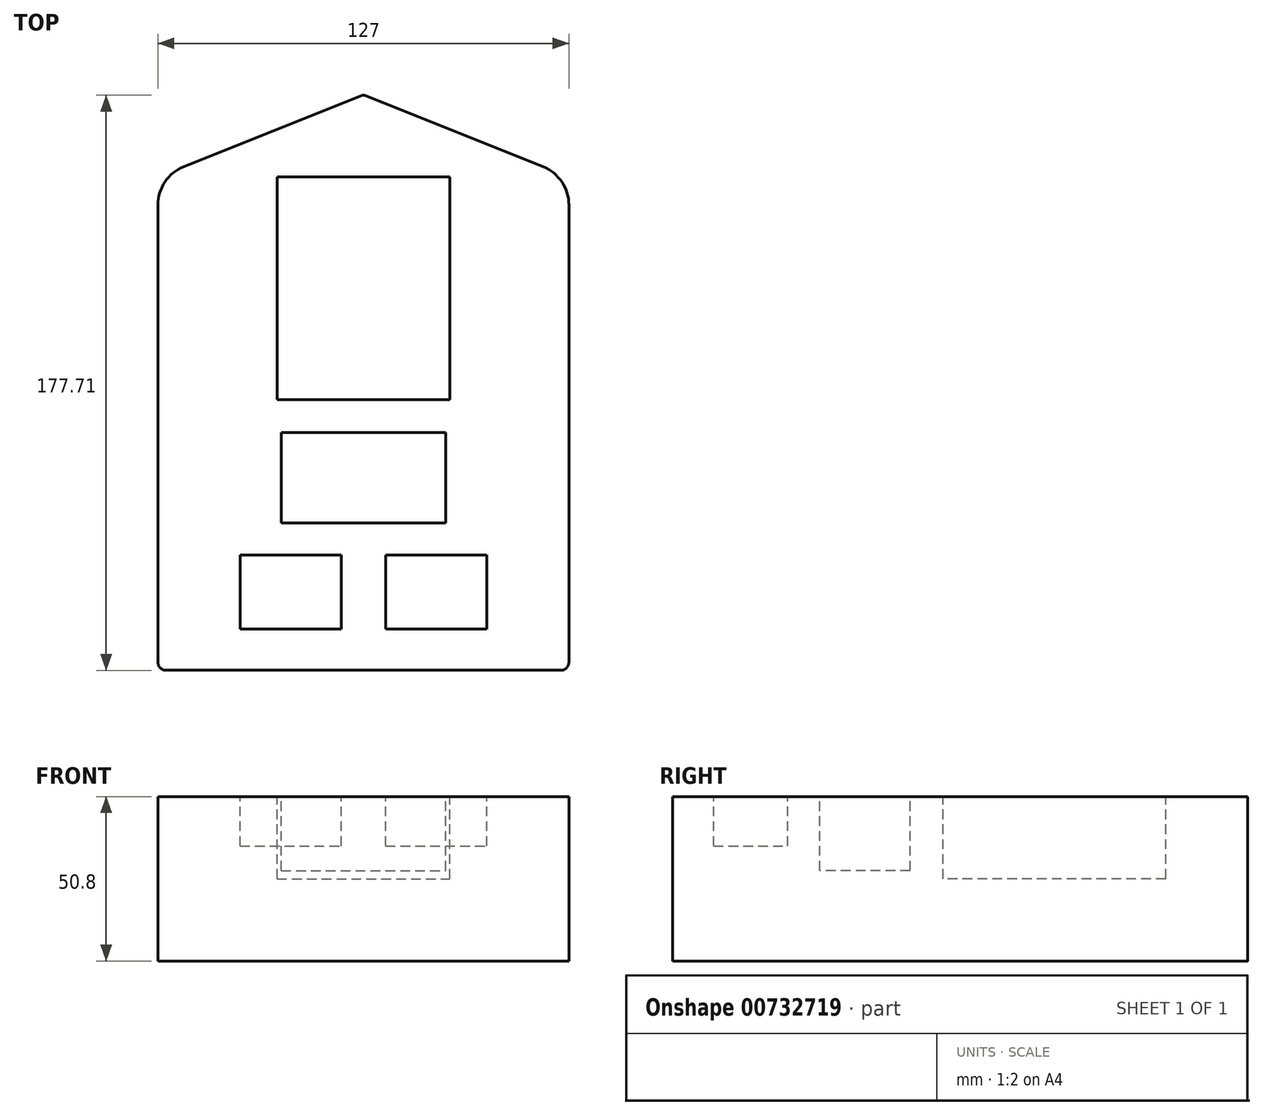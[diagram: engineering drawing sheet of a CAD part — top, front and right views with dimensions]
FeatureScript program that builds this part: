
annotation { "Feature Type Name" : "Feature", "Feature Type Description" : "" }
export const myFeature = defineFeature(function(context is Context, id is Id, definition is map)
    precondition{}
    {
        {
            var Q0;
            Q0=qCreatedBy(makeId("Top.planeOp"),FACE);
            var sketch = newSketch(context, id + "F0", { "sketchPlane" : qUnion([Q0])});
            skLineSegment(sketch, "E0.bottom", {"start": v(-191.13, -124.75) * mm, "end": v(-64.13, -124.74) * mm});
            skLineSegment(sketch, "E0.left", {"start": v(-191.13, -124.75) * mm, "end": v(-191.13, 27.65) * mm});
            skLineSegment(sketch, "E0.right", {"start": v(-64.13, -124.74) * mm, "end": v(-64.13, 27.65) * mm});
            skLineSegment(sketch, "E1", {"start": v(-191.13, 27.65) * mm, "end": v(-127.63, 53.05) * mm});
            skLineSegment(sketch, "E2", {"start": v(-127.63, 53.05) * mm, "end": v(-64.13, 27.65) * mm});
            skPoint(sketch, "E3.orphan", {"position": v(-191.13, 53.05) * mm});
            skPoint(sketch, "E0.top.end.orphan", {"position": v(-64.13, 53.05) * mm});
            skPoint(sketch, "E4", {"position": v(-191.13, 27.65) * mm});
            skPoint(sketch, "E5", {"position": v(-64.13, 27.65) * mm});
            skPoint(sketch, "E6", {"position": v(-154.3, 27.65) * mm});
            skPoint(sketch, "E7", {"position": v(-100.96, 27.65) * mm});
            skLineSegment(sketch, "E8", {"start": v(-154.3, 27.65) * mm, "end": v(-100.96, 27.65) * mm});
            skPoint(sketch, "E9", {"position": v(-191.13, -41.18) * mm});
            skPoint(sketch, "E10", {"position": v(-64.13, -41.18) * mm});
            skPoint(sketch, "E11", {"position": v(-154.3, -41.18) * mm});
            skPoint(sketch, "E12", {"position": v(-100.96, -41.18) * mm});
            skLineSegment(sketch, "E13", {"start": v(-154.3, 27.65) * mm, "end": v(-154.3, -41.18) * mm});
            skLineSegment(sketch, "E14", {"start": v(-100.96, -41.18) * mm, "end": v(-100.96, 27.65) * mm});
            skLineSegment(sketch, "E15", {"start": v(-100.96, -41.18) * mm, "end": v(-154.3, -41.18) * mm});
            skPoint(sketch, "E16", {"position": v(-165.73, -124.75) * mm});
            skPoint(sketch, "E17", {"position": v(-127.63, 27.65) * mm});
            skPoint(sketch, "E18", {"position": v(-127.63, 53.05) * mm});
            skLineSegment(sketch, "E19", {"start": v(-127.63, 53.05) * mm, "end": v(-127.63, 27.65) * mm});
            skPoint(sketch, "E20", {"position": v(-134.5, -124.75) * mm});
            skPoint(sketch, "E21", {"position": v(-120.78, -124.75) * mm});
            skPoint(sketch, "E22", {"position": v(-89.53, -124.75) * mm});
            skPoint(sketch, "E23", {"position": v(-165.73, -112.05) * mm});
            skPoint(sketch, "E24", {"position": v(-134.5, -112.05) * mm});
            skPoint(sketch, "E25", {"position": v(-165.73, -89.19) * mm});
            skPoint(sketch, "E26", {"position": v(-134.5, -89.19) * mm});
            skPoint(sketch, "E27", {"position": v(-120.78, -112.05) * mm});
            skPoint(sketch, "E28", {"position": v(-89.53, -112.05) * mm});
            skPoint(sketch, "E29", {"position": v(-120.78, -89.19) * mm});
            skPoint(sketch, "E30", {"position": v(-89.53, -89.19) * mm});
            skLineSegment(sketch, "E31", {"start": v(-165.73, -89.19) * mm, "end": v(-165.73, -112.05) * mm});
            skLineSegment(sketch, "E32", {"start": v(-134.5, -112.05) * mm, "end": v(-165.73, -112.05) * mm});
            skLineSegment(sketch, "E33", {"start": v(-134.5, -112.05) * mm, "end": v(-134.5, -89.19) * mm});
            skLineSegment(sketch, "E34", {"start": v(-165.73, -89.19) * mm, "end": v(-134.5, -89.19) * mm});
            skLineSegment(sketch, "E35", {"start": v(-120.78, -89.19) * mm, "end": v(-89.53, -89.19) * mm});
            skLineSegment(sketch, "E36", {"start": v(-89.53, -112.05) * mm, "end": v(-89.53, -89.19) * mm});
            skLineSegment(sketch, "E37", {"start": v(-89.53, -112.05) * mm, "end": v(-120.78, -112.05) * mm});
            skLineSegment(sketch, "E38", {"start": v(-120.78, -112.05) * mm, "end": v(-120.78, -89.19) * mm});
            skPoint(sketch, "E39", {"position": v(-153.03, -51.34) * mm});
            skPoint(sketch, "E40", {"position": v(-102.23, -51.34) * mm});
            skPoint(sketch, "E41", {"position": v(-153.03, -79.28) * mm});
            skPoint(sketch, "E42", {"position": v(-102.23, -79.28) * mm});
            skLineSegment(sketch, "E43", {"start": v(-153.03, -51.34) * mm, "end": v(-102.23, -51.34) * mm});
            skLineSegment(sketch, "E44", {"start": v(-102.23, -79.28) * mm, "end": v(-102.23, -51.34) * mm});
            skLineSegment(sketch, "E45", {"start": v(-153.03, -51.34) * mm, "end": v(-153.03, -79.28) * mm});
            skLineSegment(sketch, "E46", {"start": v(-153.03, -79.28) * mm, "end": v(-102.23, -79.28) * mm});
            skPoint(sketch, "E47", {"position": v(-127.63, -51.34) * mm});
            skLineSegment(sketch, "E48", {"start": v(-127.63, -51.34) * mm, "end": v(-127.63, 27.65) * mm});
            skSolve(sketch);
        }
        {
            var Q0;
            Q0=makeQuery(id+"F0.imprint","IMPRINT",FACE,{"disambiguationData":[TD([[makeQuery(id+"F0.imprint","IMPRINT",EDGE,{"derivedFrom":sQuery(id+"F0.wireOp",EDGE,"E0.bottom")}),1.0]])]});
            var Q1;
            Q1=makeQuery(id+"F0.imprint","IMPRINT",FACE,{"disambiguationData":[TD([[makeQuery(id+"F0.imprint","IMPRINT",EDGE,{"derivedFrom":sQuery(id+"F0.wireOp",EDGE,"E8")}),-1.0]])]});
            var Q2;
            Q2=makeQuery(id+"F0.imprint","IMPRINT",FACE,{"disambiguationData":[TD([[makeQuery(id+"F0.imprint","IMPRINT",EDGE,{"derivedFrom":sQuery(id+"F0.wireOp",EDGE,"E31")}),1.0]])]});
            var Q3;
            Q3=makeQuery(id+"F0.imprint","IMPRINT",FACE,{"disambiguationData":[TD([[makeQuery(id+"F0.imprint","IMPRINT",EDGE,{"derivedFrom":sQuery(id+"F0.wireOp",EDGE,"E35")}),-1.0]])]});
            var Q4;
            {var subQ1=sQuery(id+"F0.wireOp",EDGE,"E44");Q4=makeQuery(id+"F0.imprint","IMPRINT",FACE,{"disambiguationData":[TD([[makeQuery(id+"F0.imprint","IMPRINT",EDGE,{"derivedFrom":subQ1}),1.0]])]});}
            extrude(context, id + "F1", {"entities" : qUnion([Q0, Q1, Q2, Q3, Q4]), "oppositeDirection" : true, "depth" : 50.8 * mm, "offsetDistance" : 25.4 * mm});
        }
        {
            var Q0;
            Q0=makeQuery(id+"F1.opExtrude","SWEPT_EDGE",EDGE,{"disambiguationData":[OSD([sQuery(id+"F0.wireOp",EDGE,"E0.right"),sQuery(id+"F0.wireOp",EDGE,"E2")])]});
            fillet(context, id + "F2", {"entities" : qUnion([Q0]), "radius" : 12.7 * mm, "tangentPropagation" : true, "allowEdgeOverflow" : false});
        }
        {
            var Q0;
            Q0=makeQuery(id+"F1.opExtrude","SWEPT_EDGE",EDGE,{"disambiguationData":[OSD([sQuery(id+"F0.wireOp",EDGE,"E0.left"),sQuery(id+"F0.wireOp",EDGE,"E1")])]});
            fillet(context, id + "F3", {"entities" : qUnion([Q0]), "radius" : 12.7 * mm, "tangentPropagation" : true, "allowEdgeOverflow" : false});
        }
        {
            var Q0;
            Q0=makeQuery(id+"F1.opExtrude","SWEPT_EDGE",EDGE,{"disambiguationData":[OSD([sQuery(id+"F0.wireOp",EDGE,"E1"),sQuery(id+"F0.wireOp",EDGE,"E2")])]});
            fillet(context, id + "F4", {"entities" : qUnion([Q0]), "radius" : 1.27 * mm, "tangentPropagation" : true, "allowEdgeOverflow" : false});
        }
        {
            var Q0;
            Q0=makeQuery(id+"F1.opExtrude","SWEPT_EDGE",EDGE,{"disambiguationData":[OSD([sQuery(id+"F0.wireOp",EDGE,"E0.bottom"),sQuery(id+"F0.wireOp",EDGE,"E0.left")])]});
            fillet(context, id + "F5", {"entities" : qUnion([Q0]), "radius" : 2.54 * mm, "tangentPropagation" : true, "allowEdgeOverflow" : false});
        }
        {
            var Q0;
            Q0=makeQuery(id+"F1.opExtrude","SWEPT_EDGE",EDGE,{"disambiguationData":[OSD([sQuery(id+"F0.wireOp",EDGE,"E0.bottom"),sQuery(id+"F0.wireOp",EDGE,"E0.right")])]});
            fillet(context, id + "F6", {"entities" : qUnion([Q0]), "radius" : 2.54 * mm, "tangentPropagation" : true, "allowEdgeOverflow" : false});
        }
        {
            var Q0;
            Q0=makeQuery(id+"F0.imprint","IMPRINT",FACE,{"disambiguationData":[TD([[makeQuery(id+"F0.imprint","IMPRINT",EDGE,{"derivedFrom":sQuery(id+"F0.wireOp",EDGE,"E8")}),-1.0]])]});
            extrude(context, id + "F7", {"entities" : qUnion([Q0]), "operationType" : NewBodyOperationType.REMOVE, "oppositeDirection" : true, "depth" : 25.4 * mm, "offsetDistance" : 25.4 * mm});
        }
        {
            var Q0;
            Q0=makeQuery(id+"F0.imprint","IMPRINT",FACE,{"disambiguationData":[TD([[makeQuery(id+"F0.imprint","IMPRINT",EDGE,{"derivedFrom":sQuery(id+"F0.wireOp",EDGE,"E31")}),1.0]])]});
            var Q1;
            Q1=makeQuery(id+"F0.imprint","IMPRINT",FACE,{"disambiguationData":[TD([[makeQuery(id+"F0.imprint","IMPRINT",EDGE,{"derivedFrom":sQuery(id+"F0.wireOp",EDGE,"E35")}),-1.0]])]});
            extrude(context, id + "F8", {"entities" : qUnion([Q0, Q1]), "operationType" : NewBodyOperationType.REMOVE, "oppositeDirection" : true, "depth" : 15.24 * mm, "offsetDistance" : 25.4 * mm});
        }
        {
            var Q0;
            {var subQ1=sQuery(id+"F0.wireOp",EDGE,"E44");Q0=makeQuery(id+"F0.imprint","IMPRINT",FACE,{"disambiguationData":[TD([[makeQuery(id+"F0.imprint","IMPRINT",EDGE,{"derivedFrom":subQ1}),1.0]])]});}
            extrude(context, id + "F9", {"entities" : qUnion([Q0]), "operationType" : NewBodyOperationType.REMOVE, "oppositeDirection" : true, "depth" : 22.86 * mm, "offsetDistance" : 25.4 * mm});
        }
    });
